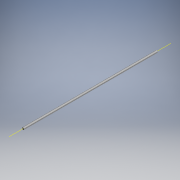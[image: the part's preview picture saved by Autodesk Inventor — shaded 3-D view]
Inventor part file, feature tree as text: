
AUTODESK INVENTOR PART (.ipt)
format: ipt  version: 2019 (Build 230136000, 136)  size: 111,616 bytes
history: native  units: mm (DEFAULTED — no unit token found)
features: extrude x1, fillet x1, sketch x1
ambient origin geometry x8: Origin, YZ Plane, XZ Plane, XY Plane, X Axis, Y Axis, Z Axis, Center Point
bodies: Solid1 (feature_tree)
feature tree (3):
  extrude  "Extrusion1"  TaperAngle=30.0deg  [1 undecoded]
  fillet  "Fillet1"  [1 undecoded]
  sketch  "Sketch1"  dims[d0=5.7658mm d1=30.0deg d2=120.0deg d3=2.883139mm d4=355.6mm d5=0.0mm d6=0.1mm d7=2.883139mm]
note: 2 required parameter values undecoded (feature->parameter linkage not recoverable at this tier; creation-order binding heuristic only, values carry confidence <= 0.55)
